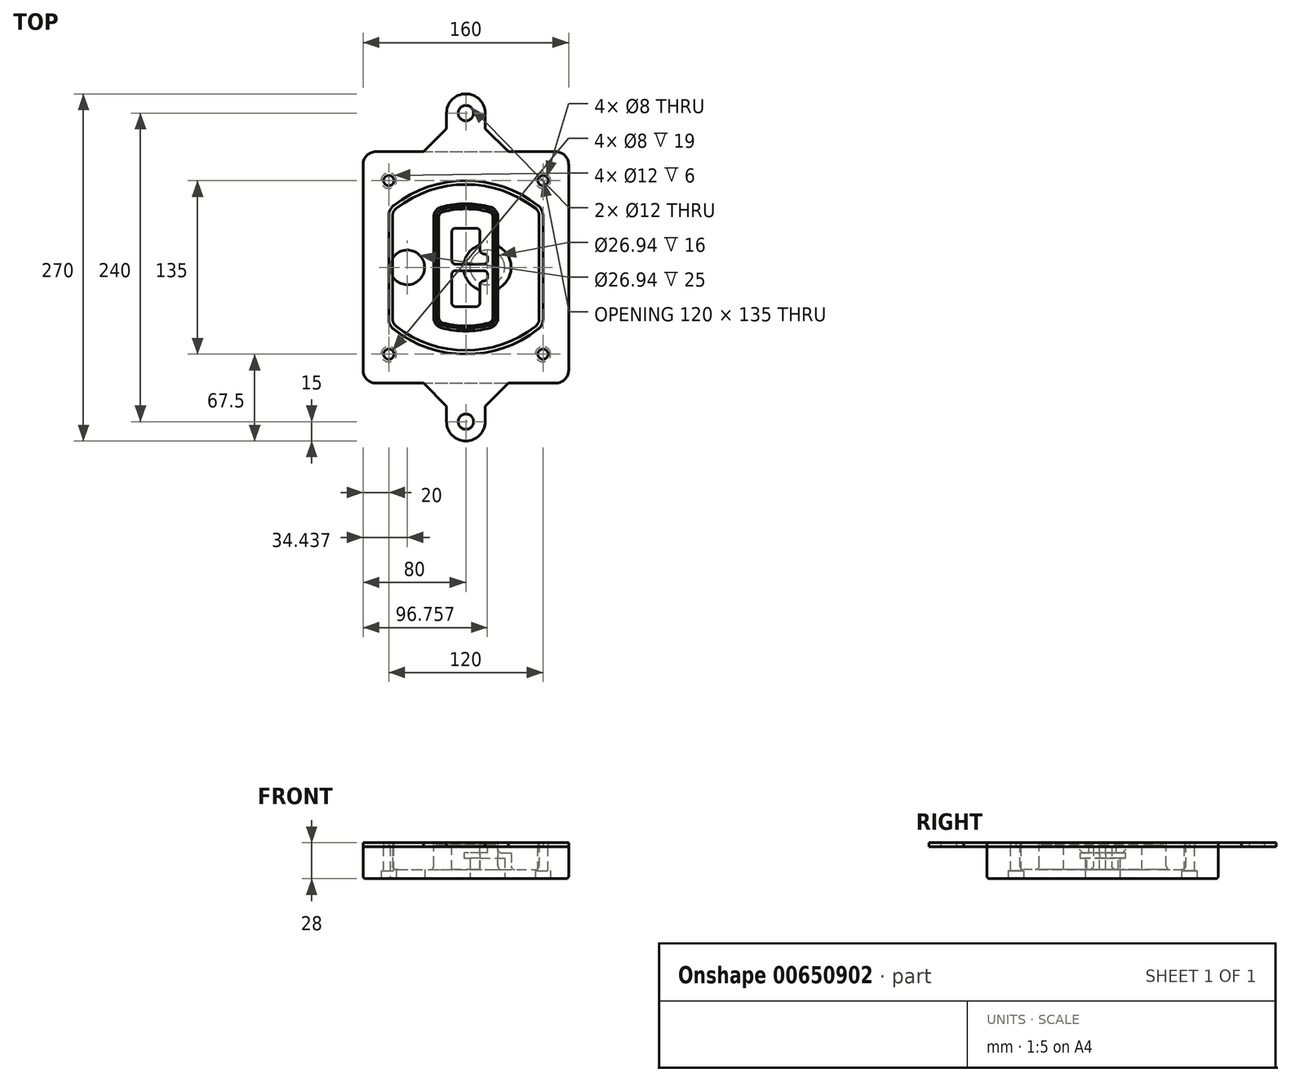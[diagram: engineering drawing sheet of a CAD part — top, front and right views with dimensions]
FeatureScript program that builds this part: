
annotation { "Feature Type Name" : "Feature", "Feature Type Description" : "" }
export const myFeature = defineFeature(function(context is Context, id is Id, definition is map)
    precondition{}
    {
        {
            var Q0;
            Q0=qCreatedBy(makeId("Top.planeOp"),FACE);
            var sketch = newSketch(context, id + "F0", { "sketchPlane" : qUnion([Q0])});
            skPoint(sketch, "E0.rect.middle", {"position": v(0, 0) * mm});
            skLineSegment(sketch, "E1.bottom", {"start": v(-70, -90) * mm, "end": v(70, -90) * mm});
            skLineSegment(sketch, "E1.top", {"start": v(-70, 90) * mm, "end": v(70, 90) * mm});
            skLineSegment(sketch, "E1.left", {"start": v(-80, -80) * mm, "end": v(-80, 80) * mm});
            skLineSegment(sketch, "E1.right", {"start": v(80, -80) * mm, "end": v(80, 80) * mm});
            skLineSegment(sketch, "E2", {"start": v(-80, 90) * mm, "end": v(80, -90) * mm, "construction": true});
            skLineSegment(sketch, "E3", {"start": v(80, 90) * mm, "end": v(-80, -90) * mm, "construction": true});
            skCircle(sketch, "E4", {"center": v(-60, 67.5) * mm, "radius": 4 * mm});
            skCircle(sketch, "E5", {"center": v(60, 67.5) * mm, "radius": 4 * mm});
            skCircle(sketch, "E6", {"center": v(60, -67.5) * mm, "radius": 4 * mm});
            skCircle(sketch, "E7", {"center": v(-60, -67.5) * mm, "radius": 4 * mm});
            skLineSegment(sketch, "E8", {"start": v(-60, 67.5) * mm, "end": v(60, 67.5) * mm, "construction": true});
            skLineSegment(sketch, "E9", {"start": v(60, 67.5) * mm, "end": v(60, -67.5) * mm, "construction": true});
            skLineSegment(sketch, "E10", {"start": v(60, -67.5) * mm, "end": v(-60, -67.5) * mm, "construction": true});
            skLineSegment(sketch, "E11", {"start": v(-60, -67.5) * mm, "end": v(-60, 67.5) * mm, "construction": true});
            skLineSegment(sketch, "E12", {"start": v(-60, 40.3) * mm, "end": v(-60, -40.3) * mm});
            skLineSegment(sketch, "E13", {"start": v(60, 40.3) * mm, "end": v(60, -40.3) * mm});
            skArc(sketch, "E14", {"start": v(56.15, 48.18) * mm, "mid": v(0, 67.5) * mm, "end": v(-56.15, 48.18) * mm});
            skArc(sketch, "E15", {"start": v(-56.15, -48.18) * mm, "mid": v(0, -67.5) * mm, "end": v(56.15, -48.18) * mm});
            skLineSegment(sketch, "E16", {"start": v(-60, 0) * mm, "end": v(60, 0) * mm, "construction": true});
            skPoint(sketch, "E17.visualSharp", {"position": v(-60, -45) * mm});
            skArc(sketch, "E17.filletArc", {"start": v(-60, -40.3) * mm, "mid": v(-58.99, -44.68) * mm, "end": v(-56.15, -48.18) * mm});
            skPoint(sketch, "E18.visualSharp", {"position": v(-60, 45) * mm});
            skArc(sketch, "E18.filletArc", {"start": v(-56.15, 48.18) * mm, "mid": v(-58.99, 44.68) * mm, "end": v(-60, 40.3) * mm});
            skPoint(sketch, "E19.visualSharp", {"position": v(60, 45) * mm});
            skArc(sketch, "E19.filletArc", {"start": v(60, 40.3) * mm, "mid": v(58.99, 44.68) * mm, "end": v(56.15, 48.18) * mm});
            skPoint(sketch, "E20.visualSharp", {"position": v(60, -45) * mm});
            skArc(sketch, "E20.filletArc", {"start": v(56.15, -48.18) * mm, "mid": v(58.99, -44.68) * mm, "end": v(60, -40.3) * mm});
            skPoint(sketch, "E21.visualSharp", {"position": v(-80, 90) * mm});
            skArc(sketch, "E21.filletArc", {"start": v(-70, 90) * mm, "mid": v(-77.07, 87.07) * mm, "end": v(-80, 80) * mm});
            skPoint(sketch, "E22.visualSharp", {"position": v(80, 90) * mm});
            skArc(sketch, "E22.filletArc", {"start": v(80, 80) * mm, "mid": v(77.07, 87.07) * mm, "end": v(70, 90) * mm});
            skPoint(sketch, "E23.visualSharp", {"position": v(80, -90) * mm});
            skArc(sketch, "E23.filletArc", {"start": v(70, -90) * mm, "mid": v(77.07, -87.07) * mm, "end": v(80, -80) * mm});
            skPoint(sketch, "E24.visualSharp", {"position": v(-80, -90) * mm});
            skArc(sketch, "E24.filletArc", {"start": v(-80, -80) * mm, "mid": v(-77.07, -87.07) * mm, "end": v(-70, -90) * mm});
            skArc(sketch, "E25.0", {"start": v(57, 40.3) * mm, "mid": v(56.3, 43.36) * mm, "end": v(54.3, 45.81) * mm});
            skLineSegment(sketch, "E25.1", {"start": v(57, 40.3) * mm, "end": v(57, -40.3) * mm});
            skArc(sketch, "E25.2", {"start": v(54.3, -45.81) * mm, "mid": v(56.3, -43.36) * mm, "end": v(57, -40.3) * mm});
            skArc(sketch, "E25.3", {"start": v(-54.3, -45.81) * mm, "mid": v(0, -64.5) * mm, "end": v(54.3, -45.81) * mm});
            skArc(sketch, "E25.4", {"start": v(-57, -40.3) * mm, "mid": v(-56.3, -43.36) * mm, "end": v(-54.3, -45.81) * mm});
            skArc(sketch, "E25.5", {"start": v(54.3, 45.81) * mm, "mid": v(0, 64.5) * mm, "end": v(-54.3, 45.81) * mm});
            skLineSegment(sketch, "E25.6", {"start": v(-57, 40.3) * mm, "end": v(-57, -40.3) * mm});
            skArc(sketch, "E25.7", {"start": v(-54.3, 45.81) * mm, "mid": v(-56.3, 43.36) * mm, "end": v(-57, 40.3) * mm});
            skArc(sketch, "E26.0", {"start": v(-58.62, 51.33) * mm, "mid": v(-62.58, 46.43) * mm, "end": v(-64, 40.3) * mm});
            skArc(sketch, "E26.1", {"start": v(58.62, 51.33) * mm, "mid": v(0, 71.5) * mm, "end": v(-58.62, 51.33) * mm});
            skArc(sketch, "E26.2", {"start": v(64, 40.3) * mm, "mid": v(62.58, 46.43) * mm, "end": v(58.62, 51.33) * mm});
            skLineSegment(sketch, "E26.3", {"start": v(64, 40.3) * mm, "end": v(64, -40.3) * mm});
            skArc(sketch, "E26.4", {"start": v(58.62, -51.33) * mm, "mid": v(62.58, -46.43) * mm, "end": v(64, -40.3) * mm});
            skLineSegment(sketch, "E26.5", {"start": v(-64, 40.3) * mm, "end": v(-64, -40.3) * mm});
            skArc(sketch, "E26.6", {"start": v(-58.62, -51.33) * mm, "mid": v(0, -71.5) * mm, "end": v(58.62, -51.33) * mm});
            skArc(sketch, "E26.7", {"start": v(-64, -40.3) * mm, "mid": v(-62.58, -46.43) * mm, "end": v(-58.62, -51.33) * mm});
            skSolve(sketch);
        }
        {
            var Q0;
            Q0=makeQuery(id+"F0.imprint","IMPRINT",FACE,{"disambiguationData":[TD([[makeQuery(id+"F0.imprint","IMPRINT",EDGE,{"derivedFrom":sQuery(id+"F0.wireOp",EDGE,"E1.bottom")}),1.0]])]});
            var Q1;
            Q1=makeQuery(id+"F0.imprint","IMPRINT",FACE,{"disambiguationData":[TD([[makeQuery(id+"F0.imprint","IMPRINT",EDGE,{"derivedFrom":sQuery(id+"F0.wireOp",EDGE,"E12")}),1.0]])]});
            var Q2;
            Q2=makeQuery(id+"F0.imprint","IMPRINT",FACE,{"disambiguationData":[TD([[makeQuery(id+"F0.imprint","IMPRINT",EDGE,{"derivedFrom":sQuery(id+"F0.wireOp",EDGE,"E25.0")}),1.0]])]});
            var Q3;
            Q3=makeQuery(id+"F0.imprint","IMPRINT",FACE,{"disambiguationData":[TD([[makeQuery(id+"F0.imprint","IMPRINT",EDGE,{"derivedFrom":sQuery(id+"F0.wireOp",EDGE,"E12")}),-1.0]])]});
            extrude(context, id + "F1", {"entities" : qUnion([Q0, Q1, Q2, Q3]), "oppositeDirection" : true, "depth" : 25 * mm});
        }
        {
            var Q0;
            Q0=makeQuery(id+"F0.imprint","IMPRINT",FACE,{"disambiguationData":[TD([[makeQuery(id+"F0.imprint","IMPRINT",EDGE,{"derivedFrom":sQuery(id+"F0.wireOp",EDGE,"E12")}),1.0]])]});
            extrude(context, id + "F2", {"entities" : qUnion([Q0]), "operationType" : NewBodyOperationType.ADD, "depth" : 3 * mm});
        }
        {
            var Q0;
            Q0=makeQuery(id+"F0.imprint","IMPRINT",FACE,{"disambiguationData":[TD([[makeQuery(id+"F0.imprint","IMPRINT",EDGE,{"derivedFrom":sQuery(id+"F0.wireOp",EDGE,"E25.0")}),1.0]])]});
            extrude(context, id + "F3", {"entities" : qUnion([Q0]), "operationType" : NewBodyOperationType.REMOVE, "oppositeDirection" : true, "depth" : 18 * mm});
        }
        {
            var Q0;
            Q0=makeQuery(id+"F2.opExtrude","CAP_FACE",FACE,{"disambiguationData":[OSD([sQuery(id+"F0.wireOp",EDGE,"E12"),sQuery(id+"F0.wireOp",EDGE,"E13"),sQuery(id+"F0.wireOp",EDGE,"E14"),sQuery(id+"F0.wireOp",EDGE,"E15"),sQuery(id+"F0.wireOp",EDGE,"E17.filletArc"),sQuery(id+"F0.wireOp",EDGE,"E18.filletArc"),sQuery(id+"F0.wireOp",EDGE,"E19.filletArc"),sQuery(id+"F0.wireOp",EDGE,"E20.filletArc"),sQuery(id+"F0.wireOp",EDGE,"E25.0"),sQuery(id+"F0.wireOp",EDGE,"E25.1"),sQuery(id+"F0.wireOp",EDGE,"E25.2"),sQuery(id+"F0.wireOp",EDGE,"E25.3"),sQuery(id+"F0.wireOp",EDGE,"E25.4"),sQuery(id+"F0.wireOp",EDGE,"E25.5"),sQuery(id+"F0.wireOp",EDGE,"E25.6"),sQuery(id+"F0.wireOp",EDGE,"E25.7")])],"isStart":false});
            var sketch = newSketch(context, id + "F4", { "sketchPlane" : qUnion([Q0])});
            skArc(sketch, "E27.0", {"start": v(-19.08, -46.97) * mm, "mid": v(0, -49.5) * mm, "end": v(19.08, -46.97) * mm});
            skArc(sketch, "E28.0", {"start": v(19.08, 46.97) * mm, "mid": v(0, 49.5) * mm, "end": v(-19.08, 46.97) * mm});
            skLineSegment(sketch, "E29", {"start": v(-25, 39.25) * mm, "end": v(-25, -39.25) * mm});
            skLineSegment(sketch, "E30", {"start": v(25, 39.25) * mm, "end": v(25, -39.25) * mm});
            skLineSegment(sketch, "E31", {"start": v(-25, 45.1) * mm, "end": v(25, 45.1) * mm, "construction": true});
            skLineSegment(sketch, "E32", {"start": v(-25, -45.1) * mm, "end": v(25, -45.1) * mm, "construction": true});
            skPoint(sketch, "E33.visualSharp", {"position": v(-25, 45.1) * mm});
            skArc(sketch, "E33.filletArc", {"start": v(-19.08, 46.97) * mm, "mid": v(-23.35, 44.11) * mm, "end": v(-25, 39.25) * mm});
            skPoint(sketch, "E34.visualSharp", {"position": v(25, 45.1) * mm});
            skArc(sketch, "E34.filletArc", {"start": v(25, 39.25) * mm, "mid": v(23.35, 44.11) * mm, "end": v(19.08, 46.97) * mm});
            skPoint(sketch, "E35.visualSharp", {"position": v(25, -45.1) * mm});
            skArc(sketch, "E35.filletArc", {"start": v(19.08, -46.97) * mm, "mid": v(23.35, -44.11) * mm, "end": v(25, -39.25) * mm});
            skPoint(sketch, "E36.visualSharp", {"position": v(-25, -45.1) * mm});
            skArc(sketch, "E36.filletArc", {"start": v(-25, -39.25) * mm, "mid": v(-23.35, -44.11) * mm, "end": v(-19.08, -46.97) * mm});
            skArc(sketch, "E37.0", {"start": v(54.3, 45.81) * mm, "mid": v(0, 64.5) * mm, "end": v(-54.3, 45.81) * mm});
            skArc(sketch, "E37.1", {"start": v(-54.3, 45.81) * mm, "mid": v(-56.3, 43.36) * mm, "end": v(-57, 40.3) * mm});
            skLineSegment(sketch, "E37.2", {"start": v(-57, 40.3) * mm, "end": v(-57, -40.3) * mm});
            skArc(sketch, "E37.3", {"start": v(-57, -40.3) * mm, "mid": v(-56.3, -43.36) * mm, "end": v(-54.3, -45.81) * mm});
            skArc(sketch, "E37.4", {"start": v(-54.3, -45.81) * mm, "mid": v(0, -64.5) * mm, "end": v(54.3, -45.81) * mm});
            skArc(sketch, "E37.5", {"start": v(54.3, -45.81) * mm, "mid": v(56.3, -43.36) * mm, "end": v(57, -40.3) * mm});
            skLineSegment(sketch, "E37.6", {"start": v(57, 40.3) * mm, "end": v(57, -40.3) * mm});
            skArc(sketch, "E37.7", {"start": v(57, 40.3) * mm, "mid": v(56.3, 43.36) * mm, "end": v(54.3, 45.81) * mm});
            skLineSegment(sketch, "E38.0", {"start": v(23, 39.25) * mm, "end": v(23, -39.25) * mm});
            skArc(sketch, "E38.1", {"start": v(18.56, -45.04) * mm, "mid": v(21.76, -42.9) * mm, "end": v(23, -39.25) * mm});
            skArc(sketch, "E38.2", {"start": v(-18.56, -45.04) * mm, "mid": v(0, -47.5) * mm, "end": v(18.56, -45.04) * mm});
            skArc(sketch, "E38.3", {"start": v(-23, -39.25) * mm, "mid": v(-21.76, -42.9) * mm, "end": v(-18.56, -45.04) * mm});
            skLineSegment(sketch, "E38.4", {"start": v(-23, 39.25) * mm, "end": v(-23, -39.25) * mm});
            skArc(sketch, "E38.5", {"start": v(23, 39.25) * mm, "mid": v(21.76, 42.9) * mm, "end": v(18.56, 45.04) * mm});
            skArc(sketch, "E38.6", {"start": v(-18.56, 45.04) * mm, "mid": v(-21.76, 42.9) * mm, "end": v(-23, 39.25) * mm});
            skArc(sketch, "E38.7", {"start": v(18.56, 45.04) * mm, "mid": v(0, 47.5) * mm, "end": v(-18.56, 45.04) * mm});
            skArc(sketch, "E39.0", {"start": v(21, 39.25) * mm, "mid": v(20.18, 41.68) * mm, "end": v(18.04, 43.1) * mm});
            skLineSegment(sketch, "E39.1", {"start": v(21, 39.25) * mm, "end": v(21, -39.25) * mm});
            skArc(sketch, "E39.2", {"start": v(18.04, -43.1) * mm, "mid": v(20.18, -41.68) * mm, "end": v(21, -39.25) * mm});
            skArc(sketch, "E39.3", {"start": v(-18.04, -43.1) * mm, "mid": v(0, -45.5) * mm, "end": v(18.04, -43.1) * mm});
            skArc(sketch, "E39.4", {"start": v(-21, -39.25) * mm, "mid": v(-20.18, -41.68) * mm, "end": v(-18.04, -43.1) * mm});
            skArc(sketch, "E39.5", {"start": v(18.04, 43.1) * mm, "mid": v(0, 45.5) * mm, "end": v(-18.04, 43.1) * mm});
            skLineSegment(sketch, "E39.6", {"start": v(-21, 39.25) * mm, "end": v(-21, -39.25) * mm});
            skArc(sketch, "E39.7", {"start": v(-18.04, 43.1) * mm, "mid": v(-20.18, 41.68) * mm, "end": v(-21, 39.25) * mm});
            skLineSegment(sketch, "E40", {"start": v(-25, 0) * mm, "end": v(25, 0) * mm, "construction": true});
            skLineSegment(sketch, "E41", {"start": v(-11, 5.5) * mm, "end": v(-11, 27.5) * mm});
            skLineSegment(sketch, "E42", {"start": v(-8, 30.5) * mm, "end": v(8, 30.5) * mm});
            skLineSegment(sketch, "E43", {"start": v(11, 27.5) * mm, "end": v(11, 13.5) * mm});
            skLineSegment(sketch, "E44", {"start": v(14, 10.5) * mm, "end": v(14, 10.5) * mm});
            skLineSegment(sketch, "E45", {"start": v(17, 7.5) * mm, "end": v(17, 5.5) * mm});
            skLineSegment(sketch, "E46", {"start": v(14, 2.5) * mm, "end": v(-8, 2.5) * mm});
            skPoint(sketch, "E47.visualSharp", {"position": v(-11, 30.5) * mm});
            skArc(sketch, "E47.filletArc", {"start": v(-8, 30.5) * mm, "mid": v(-10.12, 29.62) * mm, "end": v(-11, 27.5) * mm});
            skPoint(sketch, "E48.visualSharp", {"position": v(11, 30.5) * mm});
            skArc(sketch, "E48.filletArc", {"start": v(11, 27.5) * mm, "mid": v(10.12, 29.62) * mm, "end": v(8, 30.5) * mm});
            skPoint(sketch, "E49.visualSharp", {"position": v(11, 10.5) * mm});
            skArc(sketch, "E49.filletArc", {"start": v(11, 13.5) * mm, "mid": v(11.88, 11.38) * mm, "end": v(14, 10.5) * mm});
            skPoint(sketch, "E50.visualSharp", {"position": v(17, 10.5) * mm});
            skArc(sketch, "E50.filletArc", {"start": v(17, 7.5) * mm, "mid": v(16.12, 9.62) * mm, "end": v(14, 10.5) * mm});
            skPoint(sketch, "E51.visualSharp", {"position": v(17, 2.5) * mm});
            skArc(sketch, "E51.filletArc", {"start": v(14, 2.5) * mm, "mid": v(16.12, 3.38) * mm, "end": v(17, 5.5) * mm});
            skPoint(sketch, "E52.visualSharp", {"position": v(-11, 2.5) * mm});
            skArc(sketch, "E52.filletArc", {"start": v(-11, 5.5) * mm, "mid": v(-10.12, 3.38) * mm, "end": v(-8, 2.5) * mm});
            skLineSegment(sketch, "E53.0.MirrorCS", {"start": v(14, -2.5) * mm, "end": v(-8, -2.5) * mm});
            skArc(sketch, "E54.0.MirrorCS", {"start": v(-11, -5.5) * mm, "mid": v(-10.12, -3.38) * mm, "end": v(-8, -2.5) * mm});
            skLineSegment(sketch, "E55.0.MirrorCS", {"start": v(-11, -5.5) * mm, "end": v(-11, -27.5) * mm});
            skArc(sketch, "E56.0.MirrorCS", {"start": v(-8, -30.5) * mm, "mid": v(-10.12, -29.62) * mm, "end": v(-11, -27.5) * mm});
            skLineSegment(sketch, "E57.0.MirrorCS", {"start": v(-8, -30.5) * mm, "end": v(8, -30.5) * mm});
            skArc(sketch, "E58.0.MirrorCS", {"start": v(11, -27.5) * mm, "mid": v(10.12, -29.62) * mm, "end": v(8, -30.5) * mm});
            skLineSegment(sketch, "E59.0.MirrorCS", {"start": v(11, -27.5) * mm, "end": v(11, -13.5) * mm});
            skArc(sketch, "E60.0.MirrorCS", {"start": v(11, -13.5) * mm, "mid": v(11.88, -11.38) * mm, "end": v(14, -10.5) * mm});
            skArc(sketch, "E61.0.MirrorCS", {"start": v(17, -7.5) * mm, "mid": v(16.12, -9.62) * mm, "end": v(14, -10.5) * mm});
            skLineSegment(sketch, "E62.0.MirrorCS", {"start": v(17, -7.5) * mm, "end": v(17, -5.5) * mm});
            skArc(sketch, "E63.0.MirrorCS", {"start": v(14, -2.5) * mm, "mid": v(16.12, -3.38) * mm, "end": v(17, -5.5) * mm});
            skSolve(sketch);
        }
        {
            var Q0;
            Q0=makeQuery(id+"F4.imprint","IMPRINT",FACE,{"disambiguationData":[TD([[makeQuery(id+"F4.imprint","IMPRINT",EDGE,{"derivedFrom":sQuery(id+"F4.wireOp",EDGE,"E27.0")}),1.0]])]});
            var Q1;
            Q1=makeQuery(id+"F4.imprint","IMPRINT",FACE,{"disambiguationData":[TD([[makeQuery(id+"F4.imprint","IMPRINT",EDGE,{"derivedFrom":sQuery(id+"F4.wireOp",EDGE,"E38.0")}),-1.0]])]});
            var Q2;
            Q2=makeQuery(id+"F4.imprint","IMPRINT",FACE,{"disambiguationData":[TD([[makeQuery(id+"F4.imprint","IMPRINT",EDGE,{"derivedFrom":sQuery(id+"F4.wireOp",EDGE,"E39.0")}),1.0]])]});
            extrude(context, id + "F5", {"entities" : qUnion([Q0, Q1, Q2]), "operationType" : NewBodyOperationType.ADD, "endBound" : BoundingType.UP_TO_NEXT, "oppositeDirection" : true, "depth" : 25 * mm});
        }
        {
            var Q0;
            Q0=makeQuery(id+"F4.imprint","IMPRINT",FACE,{"disambiguationData":[TD([[makeQuery(id+"F4.imprint","IMPRINT",EDGE,{"derivedFrom":sQuery(id+"F4.wireOp",EDGE,"E38.0")}),-1.0]])]});
            extrude(context, id + "F6", {"entities" : qUnion([Q0]), "operationType" : NewBodyOperationType.REMOVE, "oppositeDirection" : true, "depth" : 2 * mm});
        }
        {
            var Q0;
            Q0=makeQuery(id+"F1.opExtrude","CAP_FACE",FACE,{"disambiguationData":[OSD([sQuery(id+"F0.wireOp",EDGE,"E1.bottom"),sQuery(id+"F0.wireOp",EDGE,"E1.top"),sQuery(id+"F0.wireOp",EDGE,"E1.left"),sQuery(id+"F0.wireOp",EDGE,"E1.right"),sQuery(id+"F0.wireOp",EDGE,"E4"),sQuery(id+"F0.wireOp",EDGE,"E5"),sQuery(id+"F0.wireOp",EDGE,"E6"),sQuery(id+"F0.wireOp",EDGE,"E7"),sQuery(id+"F0.wireOp",EDGE,"E21.filletArc"),sQuery(id+"F0.wireOp",EDGE,"E22.filletArc"),sQuery(id+"F0.wireOp",EDGE,"E23.filletArc"),sQuery(id+"F0.wireOp",EDGE,"E24.filletArc")])],"isStart":false});
            var sketch = newSketch(context, id + "F7", { "sketchPlane" : qUnion([Q0])});
            skCircle(sketch, "E64", {"center": v(16.76, 0) * mm, "radius": 13.47 * mm});
            skCircle(sketch, "E65", {"center": v(-45.56, 0) * mm, "radius": 13.47 * mm});
            skLineSegment(sketch, "E66", {"start": v(80, 0) * mm, "end": v(-80, 0) * mm});
            skCircle(sketch, "E67", {"center": v(16.76, 0) * mm, "radius": 18.47 * mm});
            skCircle(sketch, "E68", {"center": v(60, -67.5) * mm, "radius": 6 * mm});
            skCircle(sketch, "E69", {"center": v(-60, -67.5) * mm, "radius": 6 * mm});
            skCircle(sketch, "E70", {"center": v(-60, 67.5) * mm, "radius": 6 * mm});
            skCircle(sketch, "E71", {"center": v(60, 67.5) * mm, "radius": 6 * mm});
            skSolve(sketch);
        }
        {
            var Q0;
            {var subQ1=sQuery(id+"F7.wireOp",EDGE,"E66");var subQ4=sQuery(id+"F7.wireOp",EDGE,"E64");var subQ6=makeQuery(id+"F7.imprint","INTERSECT",VERTEX,{"disambiguationData":[OD(0.0)],"derivedFrom":[subQ4,subQ1]});Q0=makeQuery(id+"F7.imprint","IMPRINT",FACE,{"disambiguationData":[TD([[makeQuery(id+"F7.imprint","IMPRINT",EDGE,{"disambiguationData":[TD([[subQ6,-1.0]])],"derivedFrom":subQ4}),-1.0]])]});}
            var Q1;
            {var subQ0=sQuery(id+"F7.wireOp",EDGE,"E66");var subQ1=sQuery(id+"F7.wireOp",EDGE,"E64");var subQ3=makeQuery(id+"F7.imprint","INTERSECT",VERTEX,{"disambiguationData":[OD(0.0)],"derivedFrom":[subQ1,subQ0]});Q1=makeQuery(id+"F7.imprint","IMPRINT",FACE,{"disambiguationData":[TD([[makeQuery(id+"F7.imprint","IMPRINT",EDGE,{"disambiguationData":[TD([[subQ3,-1.0]])],"derivedFrom":subQ1}),1.0]])]});}
            var Q2;
            {var subQ0=sQuery(id+"F7.wireOp",EDGE,"E66");var subQ1=sQuery(id+"F7.wireOp",EDGE,"E64");var subQ3=makeQuery(id+"F7.imprint","INTERSECT",VERTEX,{"disambiguationData":[OD(0.0)],"derivedFrom":[subQ1,subQ0]});Q2=makeQuery(id+"F7.imprint","IMPRINT",FACE,{"disambiguationData":[TD([[makeQuery(id+"F7.imprint","IMPRINT",EDGE,{"disambiguationData":[TD([[subQ3,1.0]])],"derivedFrom":subQ1}),1.0]])]});}
            var Q3;
            {var subQ1=sQuery(id+"F7.wireOp",EDGE,"E66");var subQ4=sQuery(id+"F7.wireOp",EDGE,"E64");var subQ6=makeQuery(id+"F7.imprint","INTERSECT",VERTEX,{"disambiguationData":[OD(0.0)],"derivedFrom":[subQ4,subQ1]});Q3=makeQuery(id+"F7.imprint","IMPRINT",FACE,{"disambiguationData":[TD([[makeQuery(id+"F7.imprint","IMPRINT",EDGE,{"disambiguationData":[TD([[subQ6,1.0]])],"derivedFrom":subQ4}),-1.0]])]});}
            extrude(context, id + "F8", {"entities" : qUnion([Q0, Q1, Q2, Q3]), "operationType" : NewBodyOperationType.ADD, "oppositeDirection" : true, "depth" : 20 * mm});
        }
        {
            var Q0;
            {var subQ0=sQuery(id+"F7.wireOp",EDGE,"E66");var subQ1=sQuery(id+"F7.wireOp",EDGE,"E64");var subQ3=makeQuery(id+"F7.imprint","INTERSECT",VERTEX,{"disambiguationData":[OD(0.0)],"derivedFrom":[subQ1,subQ0]});Q0=makeQuery(id+"F7.imprint","IMPRINT",FACE,{"disambiguationData":[TD([[makeQuery(id+"F7.imprint","IMPRINT",EDGE,{"disambiguationData":[TD([[subQ3,-1.0]])],"derivedFrom":subQ1}),1.0]])]});}
            var Q1;
            {var subQ0=sQuery(id+"F7.wireOp",EDGE,"E66");var subQ1=sQuery(id+"F7.wireOp",EDGE,"E64");var subQ3=makeQuery(id+"F7.imprint","INTERSECT",VERTEX,{"disambiguationData":[OD(0.0)],"derivedFrom":[subQ1,subQ0]});Q1=makeQuery(id+"F7.imprint","IMPRINT",FACE,{"disambiguationData":[TD([[makeQuery(id+"F7.imprint","IMPRINT",EDGE,{"disambiguationData":[TD([[subQ3,1.0]])],"derivedFrom":subQ1}),1.0]])]});}
            extrude(context, id + "F9", {"entities" : qUnion([Q0, Q1]), "operationType" : NewBodyOperationType.REMOVE, "oppositeDirection" : true, "depth" : 16 * mm});
        }
        {
            var Q0;
            {var subQ0=sQuery(id+"F7.wireOp",EDGE,"E66");var subQ1=sQuery(id+"F7.wireOp",EDGE,"E65");var subQ3=makeQuery(id+"F7.imprint","INTERSECT",VERTEX,{"disambiguationData":[OD(0.0)],"derivedFrom":[subQ1,subQ0]});Q0=makeQuery(id+"F7.imprint","IMPRINT",FACE,{"disambiguationData":[TD([[makeQuery(id+"F7.imprint","IMPRINT",EDGE,{"disambiguationData":[TD([[subQ3,-1.0]])],"derivedFrom":subQ1}),1.0]])]});}
            var Q1;
            {var subQ0=sQuery(id+"F7.wireOp",EDGE,"E66");var subQ1=sQuery(id+"F7.wireOp",EDGE,"E65");var subQ3=makeQuery(id+"F7.imprint","INTERSECT",VERTEX,{"disambiguationData":[OD(0.0)],"derivedFrom":[subQ1,subQ0]});Q1=makeQuery(id+"F7.imprint","IMPRINT",FACE,{"disambiguationData":[TD([[makeQuery(id+"F7.imprint","IMPRINT",EDGE,{"disambiguationData":[TD([[subQ3,1.0]])],"derivedFrom":subQ1}),1.0]])]});}
            extrude(context, id + "F10", {"entities" : qUnion([Q0, Q1]), "operationType" : NewBodyOperationType.REMOVE, "oppositeDirection" : true, "depth" : 25 * mm});
        }
        {
            var Q0;
            Q0=makeQuery(id+"F7.imprint","IMPRINT",FACE,{"disambiguationData":[TD([[makeQuery(id+"F7.imprint","IMPRINT",EDGE,{"derivedFrom":sQuery(id+"F7.wireOp",EDGE,"E68")}),1.0]])]});
            var Q1;
            Q1=makeQuery(id+"F7.imprint","IMPRINT",FACE,{"disambiguationData":[TD([[makeQuery(id+"F7.imprint","IMPRINT",EDGE,{"derivedFrom":makeQuery(id+"F1.opExtrude","CAP_EDGE",EDGE,{"disambiguationData":[OSD([sQuery(id+"F0.wireOp",EDGE,"E5")])],"isStart":false})}),-1.0]])]});
            var Q2;
            Q2=makeQuery(id+"F7.imprint","IMPRINT",FACE,{"disambiguationData":[TD([[makeQuery(id+"F7.imprint","IMPRINT",EDGE,{"derivedFrom":sQuery(id+"F7.wireOp",EDGE,"E69")}),1.0]])]});
            var Q3;
            Q3=makeQuery(id+"F7.imprint","IMPRINT",FACE,{"disambiguationData":[TD([[makeQuery(id+"F7.imprint","IMPRINT",EDGE,{"derivedFrom":makeQuery(id+"F1.opExtrude","CAP_EDGE",EDGE,{"disambiguationData":[OSD([sQuery(id+"F0.wireOp",EDGE,"E4")])],"isStart":false})}),-1.0]])]});
            var Q4;
            Q4=makeQuery(id+"F7.imprint","IMPRINT",FACE,{"disambiguationData":[TD([[makeQuery(id+"F7.imprint","IMPRINT",EDGE,{"derivedFrom":sQuery(id+"F7.wireOp",EDGE,"E70")}),1.0]])]});
            var Q5;
            Q5=makeQuery(id+"F7.imprint","IMPRINT",FACE,{"disambiguationData":[TD([[makeQuery(id+"F7.imprint","IMPRINT",EDGE,{"derivedFrom":makeQuery(id+"F1.opExtrude","CAP_EDGE",EDGE,{"disambiguationData":[OSD([sQuery(id+"F0.wireOp",EDGE,"E7")])],"isStart":false})}),-1.0]])]});
            var Q6;
            Q6=makeQuery(id+"F7.imprint","IMPRINT",FACE,{"disambiguationData":[TD([[makeQuery(id+"F7.imprint","IMPRINT",EDGE,{"derivedFrom":sQuery(id+"F7.wireOp",EDGE,"E71")}),1.0]])]});
            var Q7;
            Q7=makeQuery(id+"F7.imprint","IMPRINT",FACE,{"disambiguationData":[TD([[makeQuery(id+"F7.imprint","IMPRINT",EDGE,{"derivedFrom":makeQuery(id+"F1.opExtrude","CAP_EDGE",EDGE,{"disambiguationData":[OSD([sQuery(id+"F0.wireOp",EDGE,"E6")])],"isStart":false})}),-1.0]])]});
            extrude(context, id + "F11", {"entities" : qUnion([Q0, Q1, Q2, Q3, Q4, Q5, Q6, Q7]), "operationType" : NewBodyOperationType.REMOVE, "oppositeDirection" : true, "depth" : 6 * mm});
        }
        {
            var Q0;
            Q0=makeQuery(id+"F9.boolean.opBoolean","COPY",FACE,{"derivedFrom":makeQuery(id+"F9.opExtrude","CAP_FACE",FACE,{"disambiguationData":[OSD([sQuery(id+"F7.wireOp",EDGE,"E64")])],"isStart":false})});
            var sketch = newSketch(context, id + "F12", { "sketchPlane" : qUnion([Q0])});
            skArc(sketch, "E72.0", {"start": v(11, 17.55) * mm, "mid": v(2.57, 11.82) * mm, "end": v(-1.54, 2.5) * mm});
            skArc(sketch, "E72.1", {"start": v(-1.54, -2.5) * mm, "mid": v(2.57, -11.82) * mm, "end": v(11, -17.55) * mm});
            skLineSegment(sketch, "E73", {"start": v(-1.54, -2.5) * mm, "end": v(14, -2.5) * mm});
            skLineSegment(sketch, "E74.0", {"start": v(14, 2.5) * mm, "end": v(-1.54, 2.5) * mm});
            skArc(sketch, "E74.1", {"start": v(14, 2.5) * mm, "mid": v(16.12, 3.38) * mm, "end": v(17, 5.5) * mm});
            skLineSegment(sketch, "E74.2", {"start": v(17, 7.5) * mm, "end": v(17, 5.5) * mm});
            skArc(sketch, "E74.3", {"start": v(17, 7.5) * mm, "mid": v(16.12, 9.62) * mm, "end": v(14, 10.5) * mm});
            skArc(sketch, "E74.4", {"start": v(11, 13.5) * mm, "mid": v(11.88, 11.38) * mm, "end": v(14, 10.5) * mm});
            skLineSegment(sketch, "E74.5", {"start": v(11, 17.55) * mm, "end": v(11, 13.5) * mm});
            skLineSegment(sketch, "E74.7", {"start": v(14, -2.5) * mm, "end": v(-1.54, -2.5) * mm});
            skArc(sketch, "E74.8", {"start": v(14, -2.5) * mm, "mid": v(16.12, -3.38) * mm, "end": v(17, -5.5) * mm});
            skLineSegment(sketch, "E74.9", {"start": v(17, -7.5) * mm, "end": v(17, -5.5) * mm});
            skArc(sketch, "E74.10", {"start": v(17, -7.5) * mm, "mid": v(16.12, -9.62) * mm, "end": v(14, -10.5) * mm});
            skArc(sketch, "E74.11", {"start": v(11, -13.5) * mm, "mid": v(11.88, -11.38) * mm, "end": v(14, -10.5) * mm});
            skLineSegment(sketch, "E74.12", {"start": v(11, -17.55) * mm, "end": v(11, -13.5) * mm});
            skPoint(sketch, "E75.orphan", {"position": v(11, -27.5) * mm});
            skPoint(sketch, "E76.orphan", {"position": v(-8, -2.5) * mm});
            skPoint(sketch, "E77.orphan", {"position": v(-8, 2.5) * mm});
            skPoint(sketch, "E78.orphan", {"position": v(11, 27.5) * mm});
            skSolve(sketch);
        }
        {
            var Q0;
            {var subQ7=sQuery(id+"F12.wireOp",EDGE,"E72.0");var subQ14=sQuery(id+"F12.wireOp",EDGE,"E72.1");var subQ16=sQuery(id+"F12.wireOp",EDGE,"E74.1");var subQ18=sQuery(id+"F12.wireOp",EDGE,"E74.8");Q0=qUnion([makeQuery(id+"F12.imprint","IMPRINT",FACE,{"disambiguationData":[TD([[makeQuery(id+"F12.imprint","IMPRINT",EDGE,{"derivedFrom":subQ7}),1.0]])]}),makeQuery(id+"F12.imprint","IMPRINT",FACE,{"disambiguationData":[TD([[makeQuery(id+"F12.imprint","IMPRINT",EDGE,{"derivedFrom":subQ14}),1.0]])]}),makeQuery(id+"F12.imprint","IMPRINT",FACE,{"disambiguationData":[TD([[makeQuery(id+"F12.imprint","IMPRINT",EDGE,{"derivedFrom":subQ16}),1.0]])]}),makeQuery(id+"F12.imprint","IMPRINT",FACE,{"disambiguationData":[TD([[makeQuery(id+"F12.imprint","IMPRINT",EDGE,{"derivedFrom":subQ18}),-1.0]])]})]);}
            var Q1;
            Q1=makeQuery(id+"F5.boolean.opBoolean","SPLIT",FACE,{"disambiguationData":[TD([makeQuery(id+"F5.opExtrude","SWEPT_FACE",FACE,{"disambiguationData":[OSD([sQuery(id+"F4.wireOp",EDGE,"E41")])]})])],"derivedFrom":makeQuery(id+"F3.boolean.opBoolean","COPY",FACE,{"derivedFrom":makeQuery(id+"F3.opExtrude","CAP_FACE",FACE,{"disambiguationData":[OSD([sQuery(id+"F0.wireOp",EDGE,"E25.0"),sQuery(id+"F0.wireOp",EDGE,"E25.1"),sQuery(id+"F0.wireOp",EDGE,"E25.2"),sQuery(id+"F0.wireOp",EDGE,"E25.3"),sQuery(id+"F0.wireOp",EDGE,"E25.4"),sQuery(id+"F0.wireOp",EDGE,"E25.5"),sQuery(id+"F0.wireOp",EDGE,"E25.6"),sQuery(id+"F0.wireOp",EDGE,"E25.7")])],"isStart":false})})});
            extrude(context, id + "F13", {"entities" : qUnion([Q0]), "operationType" : NewBodyOperationType.REMOVE, "endBound" : BoundingType.UP_TO_SURFACE, "endBoundEntityFace" : qUnion([Q1]), "depth" : 25 * mm});
        }
        {
            var Q0;
            Q0=makeQuery(id+"F3.boolean.opBoolean","COPY",EDGE,{"derivedFrom":makeQuery(id+"F3.opExtrude","CAP_EDGE",EDGE,{"disambiguationData":[OSD([sQuery(id+"F0.wireOp",EDGE,"E25.6")])],"isStart":false})});
            var Q1;
            Q1=makeQuery(id+"F8.boolean.opBoolean","INTERSECT",EDGE,{"derivedFrom":[makeQuery(id+"F5.opExtrude","SWEPT_FACE",FACE,{"disambiguationData":[OSD([sQuery(id+"F4.wireOp",EDGE,"E30")])]}),makeQuery(id+"F8.opExtrude","CAP_FACE",FACE,{"disambiguationData":[OSD([sQuery(id+"F7.wireOp",EDGE,"E67")])],"isStart":false})]});
            var Q2;
            Q2=makeQuery(id+"F8.boolean.opBoolean","INTERSECT",EDGE,{"disambiguationData":[OD(1.0)],"derivedFrom":[makeQuery(id+"F5.opExtrude","SWEPT_FACE",FACE,{"disambiguationData":[OSD([sQuery(id+"F4.wireOp",EDGE,"E30")])]}),makeQuery(id+"F8.opExtrude","SWEPT_FACE",FACE,{"disambiguationData":[OSD([sQuery(id+"F7.wireOp",EDGE,"E67")])]})]});
            var Q3;
            {var subQ0=sQuery(id+"F4.wireOp",EDGE,"E30");Q3=makeQuery(id+"F8.boolean.opBoolean","SPLIT",EDGE,{"disambiguationData":[TD([makeQuery(id+"F5.opExtrude","SWEPT_FACE",FACE,{"disambiguationData":[OSD([sQuery(id+"F4.wireOp",EDGE,"E35.filletArc")])]})])],"derivedFrom":makeQuery(id+"F5.opExtrude","CAP_EDGE",EDGE,{"disambiguationData":[OSD([subQ0])],"isStart":false})});}
            var Q4;
            {var subQ0=sQuery(id+"F0.wireOp",EDGE,"E25.7");var subQ1=sQuery(id+"F0.wireOp",EDGE,"E25.1");var subQ2=sQuery(id+"F0.wireOp",EDGE,"E25.6");var subQ3=sQuery(id+"F0.wireOp",EDGE,"E25.5");var subQ4=sQuery(id+"F0.wireOp",EDGE,"E25.4");var subQ5=sQuery(id+"F0.wireOp",EDGE,"E25.0");var subQ6=sQuery(id+"F0.wireOp",EDGE,"E25.2");var subQ7=sQuery(id+"F0.wireOp",EDGE,"E25.3");Q4=makeQuery(id+"F8.boolean.opBoolean","INTERSECT",EDGE,{"derivedFrom":[makeQuery(id+"F5.boolean.opBoolean","SPLIT",FACE,{"disambiguationData":[TD([makeQuery(id+"F2.opExtrude","SWEPT_FACE",FACE,{"disambiguationData":[OSD([subQ5])]})])],"derivedFrom":makeQuery(id+"F3.boolean.opBoolean","COPY",FACE,{"derivedFrom":makeQuery(id+"F3.opExtrude","CAP_FACE",FACE,{"disambiguationData":[OSD([subQ5,subQ1,subQ6,subQ7,subQ4,subQ3,subQ2,subQ0])],"isStart":false})})}),makeQuery(id+"F8.opExtrude","SWEPT_FACE",FACE,{"disambiguationData":[OSD([sQuery(id+"F7.wireOp",EDGE,"E67")])]})]});}
            var Q5;
            Q5=makeQuery(id+"F8.boolean.opBoolean","INTERSECT",EDGE,{"disambiguationData":[OD(0.0)],"derivedFrom":[makeQuery(id+"F5.opExtrude","SWEPT_FACE",FACE,{"disambiguationData":[OSD([sQuery(id+"F4.wireOp",EDGE,"E30")])]}),makeQuery(id+"F8.opExtrude","SWEPT_FACE",FACE,{"disambiguationData":[OSD([sQuery(id+"F7.wireOp",EDGE,"E67")])]})]});
            fillet(context, id + "F14", {"entities" : qUnion([Q0, Q1, Q2, Q3, Q4, Q5]), "radius" : 3 * mm, "tangentPropagation" : true, "allowEdgeOverflow" : false});
        }
        {
            var Q0;
            Q0=makeQuery(id+"F1.opExtrude","CAP_EDGE",EDGE,{"disambiguationData":[OSD([sQuery(id+"F0.wireOp",EDGE,"E1.bottom")])],"isStart":false});
            fillet(context, id + "F15", {"entities" : qUnion([Q0]), "radius" : 2 * mm, "tangentPropagation" : true, "allowEdgeOverflow" : false});
        }
        {
            var Q0;
            {var subQ0=sQuery(id+"F0.wireOp",EDGE,"E21.filletArc");var subQ1=sQuery(id+"F0.wireOp",EDGE,"E7");var subQ2=sQuery(id+"F0.wireOp",EDGE,"E6");var subQ3=sQuery(id+"F0.wireOp",EDGE,"E5");var subQ4=sQuery(id+"F0.wireOp",EDGE,"E4");var subQ5=sQuery(id+"F0.wireOp",EDGE,"E22.filletArc");var subQ6=sQuery(id+"F0.wireOp",EDGE,"E1.bottom");var subQ7=sQuery(id+"F0.wireOp",EDGE,"E1.right");var subQ8=sQuery(id+"F0.wireOp",EDGE,"E1.top");var subQ9=sQuery(id+"F0.wireOp",EDGE,"E1.left");var subQ10=sQuery(id+"F0.wireOp",EDGE,"E23.filletArc");var subQ11=sQuery(id+"F0.wireOp",EDGE,"E24.filletArc");Q0=makeQuery(id+"F2.boolean.opBoolean","SPLIT",FACE,{"disambiguationData":[TD([makeQuery(id+"F1.opExtrude","SWEPT_FACE",FACE,{"disambiguationData":[OSD([subQ6])]})])],"derivedFrom":makeQuery(id+"F1.opExtrude","CAP_FACE",FACE,{"disambiguationData":[OSD([subQ6,subQ8,subQ9,subQ7,subQ4,subQ3,subQ2,subQ1,subQ0,subQ5,subQ10,subQ11])],"isStart":true})});}
            var sketch = newSketch(context, id + "F16", { "sketchPlane" : qUnion([Q0])});
            skLineSegment(sketch, "E79.0", {"start": v(-70, 90) * mm, "end": v(70, 90) * mm});
            skArc(sketch, "E79.1", {"start": v(-70, 90) * mm, "mid": v(-77.07, 87.07) * mm, "end": v(-80, 80) * mm});
            skLineSegment(sketch, "E79.2", {"start": v(-80, -80) * mm, "end": v(-80, 80) * mm});
            skArc(sketch, "E79.3", {"start": v(-80, -80) * mm, "mid": v(-77.07, -87.07) * mm, "end": v(-70, -90) * mm});
            skLineSegment(sketch, "E79.4", {"start": v(-70, -90) * mm, "end": v(70, -90) * mm});
            skArc(sketch, "E79.5", {"start": v(70, -90) * mm, "mid": v(77.07, -87.07) * mm, "end": v(80, -80) * mm});
            skLineSegment(sketch, "E79.6", {"start": v(80, -80) * mm, "end": v(80, 80) * mm});
            skArc(sketch, "E79.7", {"start": v(80, 80) * mm, "mid": v(77.07, 87.07) * mm, "end": v(70, 90) * mm});
            skCircle(sketch, "E79.8", {"center": v(60, 67.5) * mm, "radius": 4 * mm});
            skCircle(sketch, "E79.9", {"center": v(-60, 67.5) * mm, "radius": 4 * mm});
            skCircle(sketch, "E79.10", {"center": v(-60, -67.5) * mm, "radius": 4 * mm});
            skArc(sketch, "E79.11", {"start": v(-56.15, -48.18) * mm, "mid": v(0, -67.5) * mm, "end": v(56.15, -48.18) * mm});
            skLineSegment(sketch, "E79.12", {"start": v(-60, 40.3) * mm, "end": v(-60, -40.3) * mm});
            skArc(sketch, "E79.13", {"start": v(-60, -40.3) * mm, "mid": v(-58.99, -44.68) * mm, "end": v(-56.15, -48.18) * mm});
            skArc(sketch, "E79.14", {"start": v(-56.15, 48.18) * mm, "mid": v(-58.99, 44.68) * mm, "end": v(-60, 40.3) * mm});
            skArc(sketch, "E79.15", {"start": v(56.15, 48.18) * mm, "mid": v(0, 67.5) * mm, "end": v(-56.15, 48.18) * mm});
            skArc(sketch, "E79.16", {"start": v(60, 40.3) * mm, "mid": v(58.99, 44.68) * mm, "end": v(56.15, 48.18) * mm});
            skLineSegment(sketch, "E79.17", {"start": v(60, 40.3) * mm, "end": v(60, -40.3) * mm});
            skArc(sketch, "E79.18", {"start": v(56.15, -48.18) * mm, "mid": v(58.99, -44.68) * mm, "end": v(60, -40.3) * mm});
            skCircle(sketch, "E79.19", {"center": v(60, -67.5) * mm, "radius": 4 * mm});
            skLineSegment(sketch, "E80", {"start": v(0, -10.29) * mm, "end": v(0, 120) * mm, "construction": true});
            skCircle(sketch, "E81", {"center": v(0, 120) * mm, "radius": 6 * mm});
            skArc(sketch, "E82", {"start": v(15, 120) * mm, "mid": v(0, 135) * mm, "end": v(-15, 120) * mm});
            skLineSegment(sketch, "E83", {"start": v(-15, 120) * mm, "end": v(-15, 108) * mm});
            skLineSegment(sketch, "E84", {"start": v(-33, 90) * mm, "end": v(-15, 108) * mm});
            skLineSegment(sketch, "E85", {"start": v(15, 120) * mm, "end": v(15, 108) * mm});
            skLineSegment(sketch, "E86", {"start": v(15, 108) * mm, "end": v(33, 90) * mm});
            skLineSegment(sketch, "E87", {"start": v(-99.82, 0) * mm, "end": v(101.83, 0) * mm, "construction": true});
            skArc(sketch, "E88.MirrorCS", {"start": v(15, -120) * mm, "mid": v(0, -135) * mm, "end": v(-15, -120) * mm});
            skLineSegment(sketch, "E89.MirrorCS", {"start": v(-15, -120) * mm, "end": v(-15, -108) * mm});
            skLineSegment(sketch, "E90.MirrorCS", {"start": v(-33, -90) * mm, "end": v(-15, -108) * mm});
            skLineSegment(sketch, "E91.MirrorCS", {"start": v(15, -108) * mm, "end": v(33, -90) * mm});
            skLineSegment(sketch, "E92.MirrorCS", {"start": v(15, -120) * mm, "end": v(15, -108) * mm});
            skCircle(sketch, "E93.MirrorC", {"center": v(0, -120) * mm, "radius": 6 * mm});
            skSolve(sketch);
        }
        {
            var Q0;
            Q0 = qSketchRegion(id + "F16", true);
            var Q1;
            Q1=makeQuery(id+"F2.opExtrude","CAP_FACE",FACE,{"disambiguationData":[OSD([sQuery(id+"F0.wireOp",EDGE,"E12"),sQuery(id+"F0.wireOp",EDGE,"E13"),sQuery(id+"F0.wireOp",EDGE,"E14"),sQuery(id+"F0.wireOp",EDGE,"E15"),sQuery(id+"F0.wireOp",EDGE,"E17.filletArc"),sQuery(id+"F0.wireOp",EDGE,"E18.filletArc"),sQuery(id+"F0.wireOp",EDGE,"E19.filletArc"),sQuery(id+"F0.wireOp",EDGE,"E20.filletArc"),sQuery(id+"F0.wireOp",EDGE,"E25.0"),sQuery(id+"F0.wireOp",EDGE,"E25.1"),sQuery(id+"F0.wireOp",EDGE,"E25.2"),sQuery(id+"F0.wireOp",EDGE,"E25.3"),sQuery(id+"F0.wireOp",EDGE,"E25.4"),sQuery(id+"F0.wireOp",EDGE,"E25.5"),sQuery(id+"F0.wireOp",EDGE,"E25.6"),sQuery(id+"F0.wireOp",EDGE,"E25.7")])],"isStart":false});
            extrude(context, id + "F17", {"entities" : qUnion([Q0]), "endBound" : BoundingType.UP_TO_SURFACE, "depth" : 25 * mm, "endBoundEntityFace" : qUnion([Q1]), "offsetDistance" : 25 * mm});
        }
    });
